FCSTD DOCUMENT  (FreeCAD 2022.709R28846 (Git))
Label: footprint_LED_matrix_8x8
License: Other
objects: Sketcher::SketchObject×5, App::Annotation×2, App::DocumentObjectGroup×1
note: 5 computed .brp shape members not serialized (recipe doc carries the construction recipe); baked Part::Feature solids carry a one-line shape summary decoded from their .brp

FEATURE [Sketcher::SketchObject] Sketch002  label="F_CrtYd_0.05"
  ArcFitTolerance = 0
  FullyConstrained = true
  TreeRank = 2091
  sketch-geometry (4):
    g0: LineSegment StartX=-2.286 StartY=16.764 StartZ=0 EndX=38.862 EndY=16.764 EndZ=0
    g1: LineSegment StartX=38.862 StartY=16.764 StartZ=0 EndX=38.862 EndY=-16.764 EndZ=0
    g2: LineSegment StartX=38.862 StartY=-16.764 StartZ=0 EndX=-2.286 EndY=-16.764 EndZ=0
    g3: LineSegment StartX=-2.286 StartY=-16.764 StartZ=0 EndX=-2.286 EndY=16.764 EndZ=0
  constraints (11):
    c: Coincident(g0,g1)
    c: Coincident(g1,g2)
    c: Coincident(g2,g3)
    c: Coincident(g3,g0)
    c: Horizontal(g0)
    c: Horizontal(g2)
    c: Vertical(g1)
    c: DistanceX(g0,g0) = 41.148
    c: DistanceY(g3,g3) = 33.528
    c: Symmetric(g0,g2,g-1)
    c: Distance(g-1,g3) = 2.286
FEATURE [App::Annotation] Text  label="Ref#_1.0mm"
  LabelText = REF**
  Position = (0,17,0)
  TreeRank = 2095
FEATURE [App::Annotation] Text001  label="Value#_0.8mm"
  LabelText = Value 
  Position = (11,-9,0)
  TreeRank = 2096
FEATURE [Sketcher::SketchObject] Sketch006  label="Pads_NPTH"
  ArcFitTolerance = 0
  FullyConstrained = true
  TreeRank = 2097
  expr: Constraints[9] = 1.6" - 0.16"
  sketch-geometry (4):
    g0: Circle CenterX=0 CenterY=13.97 CenterZ=0 NormalX=0 NormalY=0 NormalZ=1 AngleXU=0 Radius=1
    g1: Circle CenterX=0 CenterY=-13.97 CenterZ=0 NormalX=0 NormalY=0 NormalZ=1 AngleXU=0 Radius=1
    g2: Circle CenterX=36.576 CenterY=13.97 CenterZ=0 NormalX=0 NormalY=0 NormalZ=1 AngleXU=0 Radius=1
    g3: Circle CenterX=36.576 CenterY=-13.97 CenterZ=0 NormalX=0 NormalY=0 NormalZ=1 AngleXU=0 Radius=1
  constraints (11):
    c: Radius(g0) = 1
    c: PointOnObject(g0,g-2)
    c: Equal(g1,g0)
    c: Symmetric(g1,g0,g-1)
    c: Equal(g3,g0)
    c: Equal(g0,g2)
    c: Horizontal(g2,g0)
    c: Horizontal(g1,g3)
    c: Vertical(g2,g3)
    c: DistanceX(g0,g2) = 36.576
    c: DistanceY(g1,g0) = 27.94
FEATURE [Sketcher::SketchObject] Sketch008  label="F_Silks_0.16"
  ArcFitTolerance = 1e-06
  FullyConstrained = false
  TreeRank = 2099
  sketch-geometry (215):
    g0: Circle CenterX=24.2017 CenterY=-2.00747 CenterZ=0 NormalX=0 NormalY=0 NormalZ=-1 AngleXU=5e-16 Radius=1.5
    g1: Circle CenterX=24.2017 CenterY=1.97253 CenterZ=0 NormalX=0 NormalY=0 NormalZ=-1 AngleXU=5e-16 Radius=1.5
    g2: Circle CenterX=20.2217 CenterY=-2.00747 CenterZ=0 NormalX=0 NormalY=0 NormalZ=-1 AngleXU=5e-16 Radius=1.5
    g3: Circle CenterX=20.2217 CenterY=1.97253 CenterZ=0 NormalX=0 NormalY=0 NormalZ=-1 AngleXU=5e-16 Radius=1.5
    g4: Circle CenterX=16.2417 CenterY=-2.00747 CenterZ=0 NormalX=0 NormalY=0 NormalZ=-1 AngleXU=5e-16 Radius=1.5
    g5: Circle CenterX=16.2417 CenterY=1.97253 CenterZ=0 NormalX=0 NormalY=0 NormalZ=-1 AngleXU=5e-16 Radius=1.5
    g6: Circle CenterX=12.2617 CenterY=-2.00747 CenterZ=0 NormalX=0 NormalY=0 NormalZ=-1 AngleXU=5e-16 Radius=1.5
    g7: Circle CenterX=12.2617 CenterY=1.97253 CenterZ=0 NormalX=0 NormalY=0 NormalZ=-1 AngleXU=5e-16 Radius=1.5
    g8: Circle CenterX=8.2817 CenterY=-2.00747 CenterZ=0 NormalX=0 NormalY=0 NormalZ=-1 AngleXU=5e-16 Radius=1.5
    g9: Circle CenterX=8.2817 CenterY=1.97253 CenterZ=0 NormalX=0 NormalY=0 NormalZ=-1 AngleXU=5e-16 Radius=1.5
    g10: Ellipse CenterX=11.8642 CenterY=11.9994 CenterZ=0 NormalX=0 NormalY=0 NormalZ=-1 MajorRadius=0.4 MinorRadius=0.4 AngleXU=2.04918
    g11: Ellipse CenterX=16.9442 CenterY=11.9994 CenterZ=0 NormalX=0 NormalY=0 NormalZ=-1 MajorRadius=0.4 MinorRadius=0.4 AngleXU=2.04918
    g12: Ellipse CenterX=22.0242 CenterY=11.9994 CenterZ=0 NormalX=0 NormalY=0 NormalZ=-1 MajorRadius=0.4 MinorRadius=0.4 AngleXU=2.04918
    g13: Ellipse CenterX=27.1042 CenterY=11.9994 CenterZ=0 NormalX=0 NormalY=0 NormalZ=-1 MajorRadius=0.4 MinorRadius=0.4 AngleXU=2.04918
    g14: Ellipse CenterX=24.5642 CenterY=-12.0006 CenterZ=0 NormalX=0 NormalY=0 NormalZ=-1 MajorRadius=0.4 MinorRadius=0.4 AngleXU=2.04918
    g15: Ellipse CenterX=16.9442 CenterY=-12.0006 CenterZ=0 NormalX=0 NormalY=0 NormalZ=-1 MajorRadius=0.4 MinorRadius=0.4 AngleXU=2.04918
    g16: Ellipse CenterX=11.8642 CenterY=-12.0006 CenterZ=0 NormalX=0 NormalY=0 NormalZ=-1 MajorRadius=0.4 MinorRadius=0.4 AngleXU=2.04918
    g17: Ellipse CenterX=9.3242 CenterY=-12.0006 CenterZ=0 NormalX=0 NormalY=0 NormalZ=-1 MajorRadius=0.4 MinorRadius=0.4 AngleXU=2.04918
    g18: Ellipse CenterX=14.4042 CenterY=-12.0006 CenterZ=0 NormalX=0 NormalY=0 NormalZ=-1 MajorRadius=0.4 MinorRadius=0.4 AngleXU=2.04918
    g19: Ellipse CenterX=19.4842 CenterY=-12.0006 CenterZ=0 NormalX=0 NormalY=0 NormalZ=-1 MajorRadius=0.4 MinorRadius=0.4 AngleXU=2.04918
    g20: Ellipse CenterX=22.0242 CenterY=-12.0006 CenterZ=0 NormalX=0 NormalY=0 NormalZ=-1 MajorRadius=0.4 MinorRadius=0.4 AngleXU=2.04918
    g21: Ellipse CenterX=27.1042 CenterY=-12.0006 CenterZ=0 NormalX=0 NormalY=0 NormalZ=-1 MajorRadius=0.4 MinorRadius=0.4 AngleXU=2.04918
    g22: Ellipse CenterX=24.5642 CenterY=11.9994 CenterZ=0 NormalX=0 NormalY=0 NormalZ=-1 MajorRadius=0.4 MinorRadius=0.4 AngleXU=2.04918
    g23: Ellipse CenterX=19.4842 CenterY=11.9994 CenterZ=0 NormalX=0 NormalY=0 NormalZ=-1 MajorRadius=0.4 MinorRadius=0.4 AngleXU=2.04918
    g24: Ellipse CenterX=14.4042 CenterY=11.9994 CenterZ=0 NormalX=0 NormalY=0 NormalZ=-1 MajorRadius=0.4 MinorRadius=0.4 AngleXU=2.04918
    g25: Ellipse CenterX=9.3242 CenterY=11.9994 CenterZ=0 NormalX=0 NormalY=0 NormalZ=-1 MajorRadius=0.4 MinorRadius=0.4 AngleXU=2.04918
    g26: LineSegment StartX=10.2142 StartY=3.79939 StartZ=0 EndX=10.2142 EndY=4.99939 EndZ=0
    g27: LineSegment StartX=9.7042 StartY=4.99939 StartZ=0 EndX=9.7042 EndY=3.79939 EndZ=0
    g28: LineSegment StartX=10.2142 StartY=4.99939 StartZ=0 EndX=9.7042 EndY=4.99939 EndZ=0
    g29: LineSegment StartX=11.4842 StartY=3.79939 StartZ=0 EndX=11.4842 EndY=4.99939 EndZ=0
    g30: LineSegment StartX=10.9742 StartY=4.99939 StartZ=0 EndX=10.9742 EndY=3.79939 EndZ=0
    g31: LineSegment StartX=11.4842 StartY=4.99939 StartZ=0 EndX=10.9742 EndY=4.99939 EndZ=0
    g32: LineSegment StartX=12.7542 StartY=3.79939 StartZ=0 EndX=12.7542 EndY=4.99939 EndZ=0
    g33: LineSegment StartX=12.2442 StartY=4.99939 StartZ=0 EndX=12.2442 EndY=3.79939 EndZ=0
    g34: LineSegment StartX=12.7542 StartY=4.99939 StartZ=0 EndX=12.2442 EndY=4.99939 EndZ=0
    g35: LineSegment StartX=14.0242 StartY=3.79939 StartZ=0 EndX=14.0242 EndY=4.99939 EndZ=0
    g36: LineSegment StartX=13.5142 StartY=4.99939 StartZ=0 EndX=13.5142 EndY=3.79939 EndZ=0
    g37: LineSegment StartX=14.0242 StartY=4.99939 StartZ=0 EndX=13.5142 EndY=4.99939 EndZ=0
    g38: LineSegment StartX=15.2942 StartY=3.79939 StartZ=0 EndX=15.2942 EndY=4.99939 EndZ=0
    g39: LineSegment StartX=14.7842 StartY=4.99939 StartZ=0 EndX=14.7842 EndY=3.79939 EndZ=0
    g40: LineSegment StartX=15.2942 StartY=4.99939 StartZ=0 EndX=14.7842 EndY=4.99939 EndZ=0
    g41: LineSegment StartX=16.5642 StartY=3.79939 StartZ=0 EndX=16.5642 EndY=4.99939 EndZ=0
    g42: LineSegment StartX=16.0542 StartY=4.99939 StartZ=0 EndX=16.0542 EndY=3.79939 EndZ=0
    g43: LineSegment StartX=16.5642 StartY=4.99939 StartZ=0 EndX=16.0542 EndY=4.99939 EndZ=0
    g44: LineSegment StartX=17.8342 StartY=3.79939 StartZ=0 EndX=17.8342 EndY=4.99939 EndZ=0
    g45: LineSegment StartX=17.3242 StartY=4.99939 StartZ=0 EndX=17.3242 EndY=3.79939 EndZ=0
    g46: LineSegment StartX=17.8342 StartY=4.99939 StartZ=0 EndX=17.3242 EndY=4.99939 EndZ=0
    g47: LineSegment StartX=19.1042 StartY=3.79939 StartZ=0 EndX=19.1042 EndY=4.99939 EndZ=0
    g48: LineSegment StartX=18.5942 StartY=4.99939 StartZ=0 EndX=18.5942 EndY=3.79939 EndZ=0
    g49: LineSegment StartX=19.1042 StartY=4.99939 StartZ=0 EndX=18.5942 EndY=4.99939 EndZ=0
    g50: LineSegment StartX=20.3742 StartY=3.79939 StartZ=0 EndX=20.3742 EndY=4.99939 EndZ=0
    g51: LineSegment StartX=19.8642 StartY=4.99939 StartZ=0 EndX=19.8642 EndY=3.79939 EndZ=0
    g52: LineSegment StartX=20.3742 StartY=4.99939 StartZ=0 EndX=19.8642 EndY=4.99939 EndZ=0
    g53: LineSegment StartX=21.6442 StartY=3.79939 StartZ=0 EndX=21.6442 EndY=4.99939 EndZ=0
    g54: LineSegment StartX=21.1342 StartY=4.99939 StartZ=0 EndX=21.1342 EndY=3.79939 EndZ=0
    g55: LineSegment StartX=21.6442 StartY=4.99939 StartZ=0 EndX=21.1342 EndY=4.99939 EndZ=0
    g56: LineSegment StartX=22.9142 StartY=3.79939 StartZ=0 EndX=22.9142 EndY=4.99939 EndZ=0
    g57: LineSegment StartX=22.4042 StartY=4.99939 StartZ=0 EndX=22.4042 EndY=3.79939 EndZ=0
    g58: LineSegment StartX=22.9142 StartY=4.99939 StartZ=0 EndX=22.4042 EndY=4.99939 EndZ=0
    g59: LineSegment StartX=24.1842 StartY=3.79939 StartZ=0 EndX=24.1842 EndY=4.99939 EndZ=0
    g60: LineSegment StartX=23.6742 StartY=4.99939 StartZ=0 EndX=23.6742 EndY=3.79939 EndZ=0
    g61: LineSegment StartX=24.1842 StartY=4.99939 StartZ=0 EndX=23.6742 EndY=4.99939 EndZ=0
    g62: LineSegment StartX=25.4542 StartY=3.79939 StartZ=0 EndX=25.4542 EndY=4.99939 EndZ=0
    g63: LineSegment StartX=24.9442 StartY=4.99939 StartZ=0 EndX=24.9442 EndY=3.79939 EndZ=0
    g64: LineSegment StartX=25.4542 StartY=4.99939 StartZ=0 EndX=24.9442 EndY=4.99939 EndZ=0
    g65: LineSegment StartX=26.7242 StartY=3.79939 StartZ=0 EndX=26.7242 EndY=4.99939 EndZ=0
    g66: LineSegment StartX=26.2142 StartY=4.99939 StartZ=0 EndX=26.2142 EndY=3.79939 EndZ=0
    g67: LineSegment StartX=26.7242 StartY=4.99939 StartZ=0 EndX=26.2142 EndY=4.99939 EndZ=0
    g68: LineSegment StartX=9.7042 StartY=-3.80061 StartZ=0 EndX=9.7042 EndY=-5.00061 EndZ=0
    g69: LineSegment StartX=10.2142 StartY=-5.00061 StartZ=0 EndX=10.2142 EndY=-3.80061 EndZ=0
    g70: LineSegment StartX=9.7042 StartY=-5.00061 StartZ=0 EndX=10.2142 EndY=-5.00061 EndZ=0
    g71: LineSegment StartX=10.9742 StartY=-3.80061 StartZ=0 EndX=10.9742 EndY=-5.00061 EndZ=0
    g72: LineSegment StartX=11.4842 StartY=-5.00061 StartZ=0 EndX=11.4842 EndY=-3.80061 EndZ=0
    g73: LineSegment StartX=10.9742 StartY=-5.00061 StartZ=0 EndX=11.4842 EndY=-5.00061 EndZ=0
    g74: LineSegment StartX=12.2442 StartY=-3.80061 StartZ=0 EndX=12.2442 EndY=-5.00061 EndZ=0
    g75: LineSegment StartX=12.7542 StartY=-5.00061 StartZ=0 EndX=12.7542 EndY=-3.80061 EndZ=0
    g76: LineSegment StartX=12.2442 StartY=-5.00061 StartZ=0 EndX=12.7542 EndY=-5.00061 EndZ=0
    g77: LineSegment StartX=13.5142 StartY=-3.80061 StartZ=0 EndX=13.5142 EndY=-5.00061 EndZ=0
    g78: LineSegment StartX=14.0242 StartY=-5.00061 StartZ=0 EndX=14.0242 EndY=-3.80061 EndZ=0
    g79: LineSegment StartX=13.5142 StartY=-5.00061 StartZ=0 EndX=14.0242 EndY=-5.00061 EndZ=0
    g80: LineSegment StartX=14.7842 StartY=-3.80061 StartZ=0 EndX=14.7842 EndY=-5.00061 EndZ=0
    g81: LineSegment StartX=15.2942 StartY=-5.00061 StartZ=0 EndX=15.2942 EndY=-3.80061 EndZ=0
    g82: LineSegment StartX=14.7842 StartY=-5.00061 StartZ=0 EndX=15.2942 EndY=-5.00061 EndZ=0
    g83: LineSegment StartX=16.0542 StartY=-3.80061 StartZ=0 EndX=16.0542 EndY=-5.00061 EndZ=0
    g84: LineSegment StartX=16.5642 StartY=-5.00061 StartZ=0 EndX=16.5642 EndY=-3.80061 EndZ=0
    g85: LineSegment StartX=16.0542 StartY=-5.00061 StartZ=0 EndX=16.5642 EndY=-5.00061 EndZ=0
    g86: LineSegment StartX=17.3242 StartY=-3.80061 StartZ=0 EndX=17.3242 EndY=-5.00061 EndZ=0
    g87: LineSegment StartX=17.8342 StartY=-5.00061 StartZ=0 EndX=17.8342 EndY=-3.80061 EndZ=0
    g88: LineSegment StartX=17.3242 StartY=-5.00061 StartZ=0 EndX=17.8342 EndY=-5.00061 EndZ=0
    g89: LineSegment StartX=18.5942 StartY=-3.80061 StartZ=0 EndX=18.5942 EndY=-5.00061 EndZ=0
    g90: LineSegment StartX=19.1042 StartY=-5.00061 StartZ=0 EndX=19.1042 EndY=-3.80061 EndZ=0
    g91: LineSegment StartX=18.5942 StartY=-5.00061 StartZ=0 EndX=19.1042 EndY=-5.00061 EndZ=0
    g92: LineSegment StartX=19.8642 StartY=-3.80061 StartZ=0 EndX=19.8642 EndY=-5.00061 EndZ=0
    g93: LineSegment StartX=20.3742 StartY=-5.00061 StartZ=0 EndX=20.3742 EndY=-3.80061 EndZ=0
    g94: LineSegment StartX=19.8642 StartY=-5.00061 StartZ=0 EndX=20.3742 EndY=-5.00061 EndZ=0
    g95: LineSegment StartX=21.1342 StartY=-3.80061 StartZ=0 EndX=21.1342 EndY=-5.00061 EndZ=0
    g96: LineSegment StartX=21.6442 StartY=-5.00061 StartZ=0 EndX=21.6442 EndY=-3.80061 EndZ=0
    g97: LineSegment StartX=21.1342 StartY=-5.00061 StartZ=0 EndX=21.6442 EndY=-5.00061 EndZ=0
    g98: LineSegment StartX=22.4042 StartY=-3.80061 StartZ=0 EndX=22.4042 EndY=-5.00061 EndZ=0
    g99: LineSegment StartX=22.9142 StartY=-5.00061 StartZ=0 EndX=22.9142 EndY=-3.80061 EndZ=0
    g100: LineSegment StartX=22.4042 StartY=-5.00061 StartZ=0 EndX=22.9142 EndY=-5.00061 EndZ=0
    g101: LineSegment StartX=23.6742 StartY=-3.80061 StartZ=0 EndX=23.6742 EndY=-5.00061 EndZ=0
    g102: LineSegment StartX=24.1842 StartY=-5.00061 StartZ=0 EndX=24.1842 EndY=-3.80061 EndZ=0
    g103: LineSegment StartX=23.6742 StartY=-5.00061 StartZ=0 EndX=24.1842 EndY=-5.00061 EndZ=0
    g104: LineSegment StartX=24.9442 StartY=-3.80061 StartZ=0 EndX=24.9442 EndY=-5.00061 EndZ=0
    g105: LineSegment StartX=25.4542 StartY=-5.00061 StartZ=0 EndX=25.4542 EndY=-3.80061 EndZ=0
    g106: LineSegment StartX=24.9442 StartY=-5.00061 StartZ=0 EndX=25.4542 EndY=-5.00061 EndZ=0
    g107: LineSegment StartX=26.2142 StartY=-3.80061 StartZ=0 EndX=26.2142 EndY=-5.00061 EndZ=0
    g108: LineSegment StartX=26.7242 StartY=-5.00061 StartZ=0 EndX=26.7242 EndY=-3.80061 EndZ=0
    g109: LineSegment StartX=26.2142 StartY=-5.00061 StartZ=0 EndX=26.7242 EndY=-5.00061 EndZ=0
    g110: Ellipse CenterX=9.8942 CenterY=3.11939 CenterZ=0 NormalX=0 NormalY=0 NormalZ=-1 MajorRadius=0.15 MinorRadius=0.15 AngleXU=2.04918
    g111: LineSegment StartX=27.2142 StartY=-3.80061 StartZ=0 EndX=9.2142 EndY=-3.80061 EndZ=0
    g112: LineSegment StartX=27.2142 StartY=3.79939 StartZ=0 EndX=27.2142 EndY=-3.80061 EndZ=0
    g113: LineSegment StartX=9.2142 StartY=-3.80061 StartZ=0 EndX=9.2142 EndY=3.79939 EndZ=0
    g114: LineSegment StartX=9.2142 StartY=3.79939 StartZ=0 EndX=27.2142 EndY=3.79939 EndZ=0
    g115: Circle CenterX=0 CenterY=-1.27 CenterZ=0 NormalX=0 NormalY=0 NormalZ=-1 AngleXU=0 Radius=0.51
    g116: Circle CenterX=0 CenterY=3.81 CenterZ=0 NormalX=0 NormalY=0 NormalZ=-1 AngleXU=0 Radius=0.51
    g117: Circle CenterX=0 CenterY=1.27 CenterZ=0 NormalX=0 NormalY=0 NormalZ=-1 AngleXU=0 Radius=0.51
    g118: Circle CenterX=0 CenterY=-3.81 CenterZ=0 NormalX=0 NormalY=0 NormalZ=-1 AngleXU=0 Radius=0.51
    g119: Circle CenterX=36.576 CenterY=13.97 CenterZ=0 NormalX=0 NormalY=0 NormalZ=1 AngleXU=-3.14159 Radius=1
    g120: Circle CenterX=36.576 CenterY=-13.97 CenterZ=0 NormalX=0 NormalY=0 NormalZ=1 AngleXU=-3.14159 Radius=1
    g121: Circle CenterX=0 CenterY=13.97 CenterZ=0 NormalX=0 NormalY=0 NormalZ=1 AngleXU=-3.14159 Radius=1
    g122: Circle CenterX=0 CenterY=-13.97 CenterZ=0 NormalX=0 NormalY=0 NormalZ=1 AngleXU=-3.14159 Radius=1
    g123: ArcOfCircle CenterX=36.068 CenterY=13.97 CenterZ=0 NormalX=0 NormalY=0 NormalZ=1 AngleXU=1.5708 Radius=2.54 StartAngle=4.71239 EndAngle=6.28319
    g124: LineSegment StartX=0.508 StartY=16.51 StartZ=0 EndX=36.068 EndY=16.51 EndZ=0
    g125: ArcOfCircle CenterX=0.508 CenterY=13.97 CenterZ=0 NormalX=0 NormalY=0 NormalZ=1 AngleXU=3.14155 Radius=2.54 StartAngle=4.71243 EndAngle=6.28323
    g126: LineSegment StartX=-2.032 StartY=-13.97 StartZ=0 EndX=-2.032 EndY=13.97 EndZ=0
    g127: ArcOfCircle CenterX=0.508 CenterY=-13.97 CenterZ=0 NormalX=0 NormalY=0 NormalZ=1 AngleXU=-1.57084 Radius=2.54 StartAngle=4.71243 EndAngle=6.28323
    g128: LineSegment StartX=36.068 StartY=-16.51 StartZ=0 EndX=0.508 EndY=-16.51 EndZ=0
    g129: ArcOfCircle CenterX=36.068 CenterY=-13.97 CenterZ=0 NormalX=0 NormalY=0 NormalZ=1 AngleXU=-4.36332e-05 Radius=2.54 StartAngle=4.71243 EndAngle=6.28323
    g130: LineSegment StartX=38.608 StartY=13.97 StartZ=0 EndX=38.608 EndY=-13.97 EndZ=0
    g131: LineSegment StartX=34.163 StartY=15.875 StartZ=0 EndX=2.413 EndY=15.875 EndZ=0
    g132: LineSegment StartX=2.413 StartY=15.875 StartZ=0 EndX=2.413 EndY=-15.875 EndZ=0
    g133: LineSegment StartX=2.413 StartY=-15.875 StartZ=0 EndX=34.163 EndY=-15.875 EndZ=0
    g134: LineSegment StartX=34.163 StartY=-15.875 StartZ=0 EndX=34.163 EndY=15.875 EndZ=0
    g135: Circle CenterX=32.288 CenterY=14 CenterZ=0 NormalX=0 NormalY=0 NormalZ=-1 AngleXU=5e-16 Radius=1.5
    g136: Circle CenterX=28.288 CenterY=14 CenterZ=0 NormalX=0 NormalY=0 NormalZ=-1 AngleXU=5e-16 Radius=1.5
    g137: Circle CenterX=24.288 CenterY=14 CenterZ=0 NormalX=0 NormalY=0 NormalZ=-1 AngleXU=5e-16 Radius=1.5
    g138: Circle CenterX=20.288 CenterY=14 CenterZ=0 NormalX=0 NormalY=0 NormalZ=-1 AngleXU=5e-16 Radius=1.5
    g139: Circle CenterX=16.288 CenterY=14 CenterZ=0 NormalX=0 NormalY=0 NormalZ=-1 AngleXU=5e-16 Radius=1.5
    g140: Circle CenterX=12.288 CenterY=14 CenterZ=0 NormalX=0 NormalY=0 NormalZ=-1 AngleXU=5e-16 Radius=1.5
    g141: Circle CenterX=8.288 CenterY=14 CenterZ=0 NormalX=0 NormalY=0 NormalZ=-1 AngleXU=5e-16 Radius=1.5
    g142: Circle CenterX=32.288 CenterY=-14 CenterZ=0 NormalX=0 NormalY=0 NormalZ=-1 AngleXU=5e-16 Radius=1.5
    g143: Circle CenterX=32.288 CenterY=-10 CenterZ=0 NormalX=0 NormalY=0 NormalZ=-1 AngleXU=5e-16 Radius=1.5
    g144: Circle CenterX=32.288 CenterY=-6 CenterZ=0 NormalX=0 NormalY=0 NormalZ=-1 AngleXU=5e-16 Radius=1.5
    g145: Circle CenterX=32.288 CenterY=-2 CenterZ=0 NormalX=0 NormalY=0 NormalZ=-1 AngleXU=5e-16 Radius=1.5
    g146: Circle CenterX=32.288 CenterY=2 CenterZ=0 NormalX=0 NormalY=0 NormalZ=-1 AngleXU=5e-16 Radius=1.5
    g147: Circle CenterX=32.288 CenterY=6 CenterZ=0 NormalX=0 NormalY=0 NormalZ=-1 AngleXU=5e-16 Radius=1.5
    g148: Circle CenterX=32.288 CenterY=10 CenterZ=0 NormalX=0 NormalY=0 NormalZ=-1 AngleXU=5e-16 Radius=1.5
    g149: Circle CenterX=28.288 CenterY=-14 CenterZ=0 NormalX=0 NormalY=0 NormalZ=-1 AngleXU=5e-16 Radius=1.5
    g150: Circle CenterX=28.288 CenterY=-10 CenterZ=0 NormalX=0 NormalY=0 NormalZ=-1 AngleXU=5e-16 Radius=1.5
    g151: Circle CenterX=28.288 CenterY=-6 CenterZ=0 NormalX=0 NormalY=0 NormalZ=-1 AngleXU=5e-16 Radius=1.5
    g152: Circle CenterX=28.288 CenterY=-2 CenterZ=0 NormalX=0 NormalY=0 NormalZ=-1 AngleXU=5e-16 Radius=1.5
    g153: Circle CenterX=28.288 CenterY=2 CenterZ=0 NormalX=0 NormalY=0 NormalZ=-1 AngleXU=5e-16 Radius=1.5
    g154: Circle CenterX=28.288 CenterY=6 CenterZ=0 NormalX=0 NormalY=0 NormalZ=-1 AngleXU=5e-16 Radius=1.5
    g155: Circle CenterX=28.288 CenterY=10 CenterZ=0 NormalX=0 NormalY=0 NormalZ=-1 AngleXU=5e-16 Radius=1.5
    g156: Circle CenterX=24.288 CenterY=-14 CenterZ=0 NormalX=0 NormalY=0 NormalZ=-1 AngleXU=5e-16 Radius=1.5
    g157: Circle CenterX=24.288 CenterY=-10 CenterZ=0 NormalX=0 NormalY=0 NormalZ=-1 AngleXU=5e-16 Radius=1.5
    g158: Circle CenterX=24.288 CenterY=-6 CenterZ=0 NormalX=0 NormalY=0 NormalZ=-1 AngleXU=5e-16 Radius=1.5
    g159: Circle CenterX=24.288 CenterY=-2 CenterZ=0 NormalX=0 NormalY=0 NormalZ=-1 AngleXU=5e-16 Radius=1.5
    g160: Circle CenterX=24.288 CenterY=2 CenterZ=0 NormalX=0 NormalY=0 NormalZ=-1 AngleXU=5e-16 Radius=1.5
    g161: Circle CenterX=24.288 CenterY=6 CenterZ=0 NormalX=0 NormalY=0 NormalZ=-1 AngleXU=5e-16 Radius=1.5
    g162: Circle CenterX=24.288 CenterY=10 CenterZ=0 NormalX=0 NormalY=0 NormalZ=-1 AngleXU=5e-16 Radius=1.5
    g163: Circle CenterX=20.288 CenterY=-14 CenterZ=0 NormalX=0 NormalY=0 NormalZ=-1 AngleXU=5e-16 Radius=1.5
    g164: Circle CenterX=20.288 CenterY=-10 CenterZ=0 NormalX=0 NormalY=0 NormalZ=-1 AngleXU=5e-16 Radius=1.5
    g165: Circle CenterX=20.288 CenterY=-6 CenterZ=0 NormalX=0 NormalY=0 NormalZ=-1 AngleXU=5e-16 Radius=1.5
    g166: Circle CenterX=20.288 CenterY=-2 CenterZ=0 NormalX=0 NormalY=0 NormalZ=-1 AngleXU=5e-16 Radius=1.5
    g167: Circle CenterX=20.288 CenterY=2 CenterZ=0 NormalX=0 NormalY=0 NormalZ=-1 AngleXU=5e-16 Radius=1.5
    g168: Circle CenterX=20.288 CenterY=6 CenterZ=0 NormalX=0 NormalY=0 NormalZ=-1 AngleXU=5e-16 Radius=1.5
    g169: Circle CenterX=20.288 CenterY=10 CenterZ=0 NormalX=0 NormalY=0 NormalZ=-1 AngleXU=5e-16 Radius=1.5
    g170: Circle CenterX=16.288 CenterY=-14 CenterZ=0 NormalX=0 NormalY=0 NormalZ=-1 AngleXU=5e-16 Radius=1.5
    g171: Circle CenterX=16.288 CenterY=-10 CenterZ=0 NormalX=0 NormalY=0 NormalZ=-1 AngleXU=5e-16 Radius=1.5
    g172: Circle CenterX=16.288 CenterY=-6 CenterZ=0 NormalX=0 NormalY=0 NormalZ=-1 AngleXU=5e-16 Radius=1.5
    g173: Circle CenterX=16.288 CenterY=-2 CenterZ=0 NormalX=0 NormalY=0 NormalZ=-1 AngleXU=5e-16 Radius=1.5
    g174: Circle CenterX=16.288 CenterY=2 CenterZ=0 NormalX=0 NormalY=0 NormalZ=-1 AngleXU=5e-16 Radius=1.5
    g175: Circle CenterX=16.288 CenterY=6 CenterZ=0 NormalX=0 NormalY=0 NormalZ=-1 AngleXU=5e-16 Radius=1.5
    g176: Circle CenterX=16.288 CenterY=10 CenterZ=0 NormalX=0 NormalY=0 NormalZ=-1 AngleXU=5e-16 Radius=1.5
    g177: Circle CenterX=12.288 CenterY=-14 CenterZ=0 NormalX=0 NormalY=0 NormalZ=-1 AngleXU=5e-16 Radius=1.5
    g178: Circle CenterX=12.288 CenterY=-10 CenterZ=0 NormalX=0 NormalY=0 NormalZ=-1 AngleXU=5e-16 Radius=1.5
    g179: Circle CenterX=12.288 CenterY=-6 CenterZ=0 NormalX=0 NormalY=0 NormalZ=-1 AngleXU=5e-16 Radius=1.5
    g180: Circle CenterX=12.288 CenterY=-2 CenterZ=0 NormalX=0 NormalY=0 NormalZ=-1 AngleXU=5e-16 Radius=1.5
    g181: Circle CenterX=12.288 CenterY=2 CenterZ=0 NormalX=0 NormalY=0 NormalZ=-1 AngleXU=5e-16 Radius=1.5
    g182: Circle CenterX=12.288 CenterY=6 CenterZ=0 NormalX=0 NormalY=0 NormalZ=-1 AngleXU=5e-16 Radius=1.5
    g183: Circle CenterX=12.288 CenterY=10 CenterZ=0 NormalX=0 NormalY=0 NormalZ=-1 AngleXU=5e-16 Radius=1.5
    g184: Circle CenterX=8.288 CenterY=-14 CenterZ=0 NormalX=0 NormalY=0 NormalZ=-1 AngleXU=5e-16 Radius=1.5
    g185: Circle CenterX=8.288 CenterY=-10 CenterZ=0 NormalX=0 NormalY=0 NormalZ=-1 AngleXU=5e-16 Radius=1.5
    g186: Circle CenterX=8.288 CenterY=-6 CenterZ=0 NormalX=0 NormalY=0 NormalZ=-1 AngleXU=5e-16 Radius=1.5
    g187: Circle CenterX=8.288 CenterY=-2 CenterZ=0 NormalX=0 NormalY=0 NormalZ=-1 AngleXU=5e-16 Radius=1.5
    g188: Circle CenterX=8.288 CenterY=2 CenterZ=0 NormalX=0 NormalY=0 NormalZ=-1 AngleXU=5e-16 Radius=1.5
    g189: Circle CenterX=8.288 CenterY=6 CenterZ=0 NormalX=0 NormalY=0 NormalZ=-1 AngleXU=5e-16 Radius=1.5
    g190: Circle CenterX=8.288 CenterY=10 CenterZ=0 NormalX=0 NormalY=0 NormalZ=-1 AngleXU=5e-16 Radius=1.5
    g191: Circle CenterX=4.288 CenterY=-14 CenterZ=0 NormalX=0 NormalY=0 NormalZ=-1 AngleXU=5e-16 Radius=1.5
    g192: Circle CenterX=4.288 CenterY=-10 CenterZ=0 NormalX=0 NormalY=0 NormalZ=-1 AngleXU=5e-16 Radius=1.5
    g193: Circle CenterX=4.288 CenterY=-6 CenterZ=0 NormalX=0 NormalY=0 NormalZ=-1 AngleXU=5e-16 Radius=1.5
    g194: Circle CenterX=4.288 CenterY=-2 CenterZ=0 NormalX=0 NormalY=0 NormalZ=-1 AngleXU=5e-16 Radius=1.5
    g195: Circle CenterX=4.288 CenterY=2 CenterZ=0 NormalX=0 NormalY=0 NormalZ=-1 AngleXU=5e-16 Radius=1.5
    g196: Circle CenterX=4.288 CenterY=6 CenterZ=0 NormalX=0 NormalY=0 NormalZ=-1 AngleXU=5e-16 Radius=1.5
    g197: Circle CenterX=4.288 CenterY=10 CenterZ=0 NormalX=0 NormalY=0 NormalZ=-1 AngleXU=5e-16 Radius=1.5
    g198: Circle CenterX=4.288 CenterY=14 CenterZ=0 NormalX=0 NormalY=0 NormalZ=-1 AngleXU=5e-16 Radius=1.5
    g199: LineSegment [constr] StartX=4.288 StartY=-14 StartZ=0 EndX=4.288 EndY=-10 EndZ=0
    g200: LineSegment [constr] StartX=4.288 StartY=-10 StartZ=0 EndX=4.288 EndY=-6 EndZ=0
    g201: LineSegment [constr] StartX=4.288 StartY=-2 StartZ=0 EndX=4.288 EndY=2 EndZ=0
    g202: LineSegment [constr] StartX=4.288 StartY=2 StartZ=0 EndX=4.288 EndY=6 EndZ=0
    g203: LineSegment [constr] StartX=4.288 StartY=6 StartZ=0 EndX=4.288 EndY=10 EndZ=0
    g204: LineSegment [constr] StartX=4.288 StartY=10 StartZ=0 EndX=4.288 EndY=14 EndZ=0
    g205: LineSegment [constr] StartX=4.288 StartY=14 StartZ=0 EndX=8.288 EndY=14 EndZ=0
    g206: LineSegment [constr] StartX=8.288 StartY=14 StartZ=0 EndX=12.288 EndY=14 EndZ=0
    g207: LineSegment [constr] StartX=12.288 StartY=14 StartZ=0 EndX=16.288 EndY=14 EndZ=0
    g208: LineSegment [constr] StartX=16.288 StartY=14 StartZ=0 EndX=20.288 EndY=14 EndZ=0
    g209: LineSegment [constr] StartX=20.288 StartY=14 StartZ=0 EndX=24.288 EndY=14 EndZ=0
    g210: LineSegment [constr] StartX=24.288 StartY=14 StartZ=0 EndX=28.288 EndY=14 EndZ=0
    g211: LineSegment [constr] StartX=28.288 StartY=14 StartZ=0 EndX=32.288 EndY=14 EndZ=0
    g212: LineSegment [constr] StartX=4.288 StartY=-14 StartZ=0 EndX=2.413 EndY=-14 EndZ=0
    g213: LineSegment [constr] StartX=4.288 StartY=-14 StartZ=0 EndX=4.288 EndY=-15.875 EndZ=0
    g214: LineSegment [constr] StartX=4.288 StartY=-2 StartZ=0 EndX=4.288 EndY=-6 EndZ=0
  constraints (277):
    c: Equal(g127,g129)
    c: Equal(g129,g123)
    c: Equal(g123,g125)
    c: Radius(g125) = 2.54
    c: Vertical(g126)
    c: Vertical(g130)
    c: Horizontal(g124)
    c: Tangent(g127,g128) = 1.5708
    c: Tangent(g126,g127) = 1.5708
    c: Tangent(g128,g129) = 1.5708
    c: Tangent(g129,g130) = 1.5708
    c: Tangent(g123,g130) = 1.5708
    c: Tangent(g123,g124) = 1.5708
    c: Tangent(g124,g125) = 1.5708
    c: Tangent(g125,g126) = 1.5708
    c: DistanceX(g125,g123) = 40.64
    c: DistanceY(g127,g124) = 33.02
    c: Symmetric(g124,g127,g-1)
    c: Distance(g-1,g126) = 2.032
    c: Diameter(g116) = 1.02
    c: Equal(g116,g117)
    c: Equal(g116,g115)
    c: Equal(g116,g118)
    c: Vertical(g116,g117)
    c: Vertical(g115,g118)
    c: DistanceY(g118,g115) = 2.54
    c: DistanceY(g115,g117) = 2.54
    c: DistanceY(g117,g116) = 2.54
    c: Symmetric(g117,g115,g-1)
    c: PointOnObject(g117,g-2)
    c: Diameter(g121) = 2
    c: Equal(g121,g119)
    c: Equal(g121,g120)
    c: Equal(g121,g122)
    c: Horizontal(g122,g120)
    c: Vertical(g120,g119)
    c: Horizontal(g119,g121)
    c: Symmetric(g122,g121,g-1)
    c: PointOnObject(g121,g-2)
    c: DistanceY(g122,g121) = 27.94
    c: Distance(g120,g130) = 2.032
    c: Diameter(g198) = 3
    c: Equal(g198,g141)
    c: Equal(g198,g140)
    c: Equal(g198,g139)
    c: Equal(g198,g138)
    c: Equal(g198,g137)
    c: Equal(g198,g136)
    c: Equal(g198,g135)
    c: Equal(g198,g148)
    c: Equal(g198,g155)
    c: Equal(g198,g162)
    c: Equal(g198,g169)
    c: Equal(g198,g176)
    c: Equal(g198,g183)
    c: Equal(g198,g190)
    c: Equal(g198,g197)
    c: Equal(g198,g196)
    c: Equal(g198,g189)
    c: Equal(g198,g182)
    c: Equal(g198,g175)
    c: Equal(g198,g168)
    c: Equal(g198,g161)
    c: Equal(g198,g154)
    c: Equal(g198,g147)
    c: Equal(g198,g146)
    c: Equal(g198,g153)
    c: Equal(g198,g160)
    c: Equal(g198,g167)
    c: Equal(g198,g174)
    c: Equal(g198,g181)
    c: Equal(g198,g188)
    c: Equal(g198,g195)
    c: Equal(g198,g194)
    c: Equal(g198,g187)
    c: Equal(g198,g180)
    c: Equal(g198,g173)
    c: Equal(g198,g166)
    c: Equal(g198,g159)
    c: Equal(g198,g152)
    c: Equal(g198,g145)
    c: Equal(g198,g144)
    c: Equal(g198,g151)
    c: Equal(g198,g158)
    c: Equal(g198,g165)
    c: Equal(g198,g172)
    c: Equal(g198,g179)
    c: Equal(g198,g186)
    c: Equal(g198,g193)
    c: Equal(g198,g192)
    c: Equal(g198,g185)
    c: Equal(g198,g178)
    c: Equal(g198,g171)
    c: Equal(g198,g164)
    c: Equal(g198,g157)
    c: Equal(g198,g150)
    c: Equal(g198,g143)
    c: Equal(g198,g142)
    c: Equal(g198,g149)
    c: Equal(g198,g156)
    c: Equal(g198,g163)
    c: Equal(g198,g170)
    c: Equal(g198,g177)
    c: Equal(g198,g184)
    c: Equal(g198,g191)
    c: Coincident(g199,g191)
    c: Coincident(g199,g192)
    c: Vertical(g199)
    c: Coincident(g200,g192)
    c: Coincident(g200,g193)
    c: Vertical(g200)
    c: Coincident(g201,g194)
    c: Coincident(g201,g195)
    c: Coincident(g202,g195)
    c: Coincident(g202,g196)
    c: Vertical(g202)
    c: Coincident(g203,g196)
    c: Coincident(g203,g197)
    c: Vertical(g203)
    c: Coincident(g204,g197)
    c: Coincident(g204,g198)
    c: Vertical(g204)
    c: Coincident(g205,g198)
    c: Coincident(g205,g141)
    c: Horizontal(g205)
    c: Coincident(g206,g141)
    c: Coincident(g206,g140)
    c: Horizontal(g206)
    c: Coincident(g207,g140)
    c: Coincident(g207,g139)
    c: Coincident(g208,g139)
    c: Coincident(g208,g138)
    c: Horizontal(g208)
    c: Coincident(g209,g138)
    c: Coincident(g209,g137)
    c: Coincident(g210,g137)
    c: Coincident(g210,g136)
    c: Horizontal(g210)
    c: Coincident(g211,g136)
    c: Coincident(g211,g135)
    c: Horizontal(g211)
    c: Equal(g199,g200)
    c: Equal(g201,g202)
    c: Equal(g202,g203)
    c: Equal(g203,g204)
    c: Equal(g205,g206)
    c: Equal(g206,g207)
    c: Equal(g207,g208)
    c: Equal(g208,g209)
    c: Equal(g209,g210)
    c: Equal(g210,g211)
    c: Symmetric(g194,g195,g-1)
    c: DistanceY(g201,g201) = 4
    c: DistanceX(g205,g205) = 4
    c: Vertical(g184,g185)
    c: Vertical(g185,g186)
    c: Vertical(g186,g187)
    c: Vertical(g187,g188)
    c: Vertical(g188,g189)
    c: Vertical(g189,g190)
    c: Vertical(g190,g141)
    c: Vertical(g140,g183)
    c: Vertical(g183,g182)
    c: Vertical(g182,g181)
    c: Vertical(g181,g180)
    c: Vertical(g180,g179)
    c: Vertical(g179,g178)
    c: Vertical(g178,g177)
    c: Vertical(g139,g176)
    c: Vertical(g176,g175)
    c: Vertical(g175,g174)
    c: Vertical(g174,g173)
    c: Vertical(g173,g172)
    c: Vertical(g172,g171)
    c: Vertical(g171,g170)
    c: Vertical(g138,g169)
    c: Vertical(g169,g168)
    c: Vertical(g168,g167)
    c: Vertical(g167,g166)
    c: Vertical(g166,g165)
    c: Vertical(g165,g164)
    c: Vertical(g164,g163)
    c: Vertical(g137,g162)
    c: Vertical(g162,g161)
    c: Vertical(g161,g160)
    c: Vertical(g160,g159)
    c: Vertical(g159,g158)
    c: Vertical(g158,g157)
    c: Vertical(g157,g156)
    c: Vertical(g136,g155)
    c: Vertical(g155,g154)
    c: Vertical(g154,g153)
    c: Vertical(g153,g152)
    c: Vertical(g152,g151)
    c: Vertical(g151,g150)
    c: Vertical(g150,g149)
    c: Vertical(g135,g148)
    c: Vertical(g148,g147)
    c: Vertical(g147,g146)
    c: Vertical(g146,g145)
    c: Vertical(g145,g144)
    c: Vertical(g144,g143)
    c: Vertical(g143,g142)
    c: Horizontal(g197,g190)
    c: Horizontal(g190,g183)
    c: Horizontal(g183,g176)
    c: Horizontal(g176,g169)
    c: Horizontal(g169,g162)
    c: Horizontal(g162,g155)
    c: Horizontal(g155,g148)
    c: Horizontal(g196,g189)
    c: Horizontal(g189,g182)
    c: Horizontal(g182,g175)
    c: Horizontal(g175,g168)
    c: Horizontal(g168,g161)
    c: Horizontal(g161,g154)
    c: Horizontal(g154,g147)
    c: Horizontal(g195,g188)
    c: Horizontal(g188,g181)
    c: Horizontal(g181,g174)
    c: Horizontal(g174,g167)
    c: Horizontal(g167,g160)
    c: Horizontal(g160,g153)
    c: Horizontal(g153,g146)
    c: Horizontal(g194,g187)
    c: Horizontal(g187,g180)
    c: Horizontal(g180,g173)
    c: Horizontal(g173,g166)
    c: Horizontal(g166,g159)
    c: Horizontal(g159,g152)
    c: Horizontal(g152,g145)
    c: Horizontal(g193,g186)
    c: Horizontal(g186,g179)
    c: Horizontal(g179,g172)
    c: Horizontal(g172,g165)
    c: Horizontal(g165,g158)
    c: Horizontal(g158,g151)
    c: Horizontal(g151,g144)
    c: Horizontal(g192,g185)
    c: Horizontal(g185,g178)
    c: Horizontal(g178,g171)
    c: Horizontal(g171,g164)
    c: Horizontal(g164,g157)
    c: Horizontal(g157,g150)
    c: Horizontal(g150,g143)
    c: Horizontal(g191,g184)
    c: Horizontal(g184,g177)
    c: Horizontal(g177,g170)
    c: Horizontal(g170,g163)
    c: Horizontal(g163,g156)
    c: Horizontal(g156,g149)
    c: Horizontal(g149,g142)
    c: Coincident(g131,g132)
    c: Horizontal(g131)
    c: Coincident(g132,g133)
    c: Horizontal(g133)
    c: Coincident(g133,g134)
    c: Vertical(g134)
    c: Coincident(g131,g134)
    c: Equal(g132,g131)
    c: DistanceY(g132,g132) = 31.75
    c: Symmetric(g131,g132,g-1)
    c: Coincident(g212,g191)
    c: PointOnObject(g212,g132)
    c: Coincident(g213,g191)
    c: PointOnObject(g213,g133)
    c: Vertical(g213)
    c: Horizontal(g212)
    c: Equal(g212,g213)
    c: DistanceX(g212,g212) = 1.875
    c: Coincident(g214,g194)
    c: Coincident(g214,g193)
    c: Vertical(g214)
    c: Horizontal(g207)
    c: Horizontal(g209)
    c: DistanceX(g125,g131) = 4.445
    c: Equal(g201,g214)
FEATURE [Sketcher::SketchObject] Sketch009  label="Pads_TH_SMD"
  ArcFitTolerance = 0
  FullyConstrained = true
  TreeRank = 2144
  sketch-geometry (8):
    g0: Circle CenterX=0 CenterY=1.27 CenterZ=0 NormalX=0 NormalY=0 NormalZ=1 AngleXU=0 Radius=0.5
    g1: Circle CenterX=0 CenterY=1.27 CenterZ=0 NormalX=0 NormalY=0 NormalZ=1 AngleXU=0 Radius=0.9
    g2: Circle CenterX=0 CenterY=-1.27 CenterZ=0 NormalX=0 NormalY=0 NormalZ=1 AngleXU=0 Radius=0.5
    g3: Circle CenterX=0 CenterY=-1.27 CenterZ=0 NormalX=0 NormalY=0 NormalZ=1 AngleXU=0 Radius=0.9
    g4: Circle CenterX=0 CenterY=-3.81 CenterZ=0 NormalX=0 NormalY=0 NormalZ=1 AngleXU=0 Radius=0.5
    g5: Circle CenterX=0 CenterY=-3.81 CenterZ=0 NormalX=0 NormalY=0 NormalZ=1 AngleXU=0 Radius=0.9
    g6: Circle CenterX=0 CenterY=3.81 CenterZ=0 NormalX=0 NormalY=0 NormalZ=1 AngleXU=0 Radius=0.5
    g7: Circle CenterX=0 CenterY=3.81 CenterZ=0 NormalX=0 NormalY=0 NormalZ=1 AngleXU=0 Radius=0.9
  constraints (18):
    c: Diameter(g0) = 1
    c: Diameter(g1) = 1.8
    c: DistanceX(g0,g-1) = 0
    c: Coincident(g0,g1)
    c: DistanceY(g-1,g0) = 1.27
    c: Equal(g3,g1)
    c: Equal(g2,g0)
    c: Coincident(g2,g3)
    c: Symmetric(g2,g0,g-1)
    c: Equal(g4,g0)
    c: Equal(g5,g1)
    c: Coincident(g4,g5)
    c: PointOnObject(g4,g-2)
    c: DistanceY(g4,g2) = 2.54
    c: Coincident(g6,g7)
    c: Equal(g6,g0)
    c: Equal(g7,g1)
    c: Symmetric(g6,g4,g-1)
FEATURE [Sketcher::SketchObject] Sketch010  label="F_Fab_0.1"
  ArcFitTolerance = 1e-06
  FullyConstrained = false
  TreeRank = 2146
  sketch-geometry (215):
    g0: Circle CenterX=24.2017 CenterY=-2.00747 CenterZ=0 NormalX=0 NormalY=0 NormalZ=-1 AngleXU=5e-16 Radius=1.5
    g1: Circle CenterX=24.2017 CenterY=1.97253 CenterZ=0 NormalX=0 NormalY=0 NormalZ=-1 AngleXU=5e-16 Radius=1.5
    g2: Circle CenterX=20.2217 CenterY=-2.00747 CenterZ=0 NormalX=0 NormalY=0 NormalZ=-1 AngleXU=5e-16 Radius=1.5
    g3: Circle CenterX=20.2217 CenterY=1.97253 CenterZ=0 NormalX=0 NormalY=0 NormalZ=-1 AngleXU=5e-16 Radius=1.5
    g4: Circle CenterX=16.2417 CenterY=-2.00747 CenterZ=0 NormalX=0 NormalY=0 NormalZ=-1 AngleXU=5e-16 Radius=1.5
    g5: Circle CenterX=16.2417 CenterY=1.97253 CenterZ=0 NormalX=0 NormalY=0 NormalZ=-1 AngleXU=5e-16 Radius=1.5
    g6: Circle CenterX=12.2617 CenterY=-2.00747 CenterZ=0 NormalX=0 NormalY=0 NormalZ=-1 AngleXU=5e-16 Radius=1.5
    g7: Circle CenterX=12.2617 CenterY=1.97253 CenterZ=0 NormalX=0 NormalY=0 NormalZ=-1 AngleXU=5e-16 Radius=1.5
    g8: Circle CenterX=8.2817 CenterY=-2.00747 CenterZ=0 NormalX=0 NormalY=0 NormalZ=-1 AngleXU=5e-16 Radius=1.5
    g9: Circle CenterX=8.2817 CenterY=1.97253 CenterZ=0 NormalX=0 NormalY=0 NormalZ=-1 AngleXU=5e-16 Radius=1.5
    g10: Ellipse CenterX=11.8642 CenterY=11.9994 CenterZ=0 NormalX=0 NormalY=0 NormalZ=-1 MajorRadius=0.4 MinorRadius=0.4 AngleXU=2.04918
    g11: Ellipse CenterX=16.9442 CenterY=11.9994 CenterZ=0 NormalX=0 NormalY=0 NormalZ=-1 MajorRadius=0.4 MinorRadius=0.4 AngleXU=2.04918
    g12: Ellipse CenterX=22.0242 CenterY=11.9994 CenterZ=0 NormalX=0 NormalY=0 NormalZ=-1 MajorRadius=0.4 MinorRadius=0.4 AngleXU=2.04918
    g13: Ellipse CenterX=27.1042 CenterY=11.9994 CenterZ=0 NormalX=0 NormalY=0 NormalZ=-1 MajorRadius=0.4 MinorRadius=0.4 AngleXU=2.04918
    g14: Ellipse CenterX=24.5642 CenterY=-12.0006 CenterZ=0 NormalX=0 NormalY=0 NormalZ=-1 MajorRadius=0.4 MinorRadius=0.4 AngleXU=2.04918
    g15: Ellipse CenterX=16.9442 CenterY=-12.0006 CenterZ=0 NormalX=0 NormalY=0 NormalZ=-1 MajorRadius=0.4 MinorRadius=0.4 AngleXU=2.04918
    g16: Ellipse CenterX=11.8642 CenterY=-12.0006 CenterZ=0 NormalX=0 NormalY=0 NormalZ=-1 MajorRadius=0.4 MinorRadius=0.4 AngleXU=2.04918
    g17: Ellipse CenterX=9.3242 CenterY=-12.0006 CenterZ=0 NormalX=0 NormalY=0 NormalZ=-1 MajorRadius=0.4 MinorRadius=0.4 AngleXU=2.04918
    g18: Ellipse CenterX=14.4042 CenterY=-12.0006 CenterZ=0 NormalX=0 NormalY=0 NormalZ=-1 MajorRadius=0.4 MinorRadius=0.4 AngleXU=2.04918
    g19: Ellipse CenterX=19.4842 CenterY=-12.0006 CenterZ=0 NormalX=0 NormalY=0 NormalZ=-1 MajorRadius=0.4 MinorRadius=0.4 AngleXU=2.04918
    g20: Ellipse CenterX=22.0242 CenterY=-12.0006 CenterZ=0 NormalX=0 NormalY=0 NormalZ=-1 MajorRadius=0.4 MinorRadius=0.4 AngleXU=2.04918
    g21: Ellipse CenterX=27.1042 CenterY=-12.0006 CenterZ=0 NormalX=0 NormalY=0 NormalZ=-1 MajorRadius=0.4 MinorRadius=0.4 AngleXU=2.04918
    g22: Ellipse CenterX=24.5642 CenterY=11.9994 CenterZ=0 NormalX=0 NormalY=0 NormalZ=-1 MajorRadius=0.4 MinorRadius=0.4 AngleXU=2.04918
    g23: Ellipse CenterX=19.4842 CenterY=11.9994 CenterZ=0 NormalX=0 NormalY=0 NormalZ=-1 MajorRadius=0.4 MinorRadius=0.4 AngleXU=2.04918
    g24: Ellipse CenterX=14.4042 CenterY=11.9994 CenterZ=0 NormalX=0 NormalY=0 NormalZ=-1 MajorRadius=0.4 MinorRadius=0.4 AngleXU=2.04918
    g25: Ellipse CenterX=9.3242 CenterY=11.9994 CenterZ=0 NormalX=0 NormalY=0 NormalZ=-1 MajorRadius=0.4 MinorRadius=0.4 AngleXU=2.04918
    g26: LineSegment StartX=10.2142 StartY=3.79939 StartZ=0 EndX=10.2142 EndY=4.99939 EndZ=0
    g27: LineSegment StartX=9.7042 StartY=4.99939 StartZ=0 EndX=9.7042 EndY=3.79939 EndZ=0
    g28: LineSegment StartX=10.2142 StartY=4.99939 StartZ=0 EndX=9.7042 EndY=4.99939 EndZ=0
    g29: LineSegment StartX=11.4842 StartY=3.79939 StartZ=0 EndX=11.4842 EndY=4.99939 EndZ=0
    g30: LineSegment StartX=10.9742 StartY=4.99939 StartZ=0 EndX=10.9742 EndY=3.79939 EndZ=0
    g31: LineSegment StartX=11.4842 StartY=4.99939 StartZ=0 EndX=10.9742 EndY=4.99939 EndZ=0
    g32: LineSegment StartX=12.7542 StartY=3.79939 StartZ=0 EndX=12.7542 EndY=4.99939 EndZ=0
    g33: LineSegment StartX=12.2442 StartY=4.99939 StartZ=0 EndX=12.2442 EndY=3.79939 EndZ=0
    g34: LineSegment StartX=12.7542 StartY=4.99939 StartZ=0 EndX=12.2442 EndY=4.99939 EndZ=0
    g35: LineSegment StartX=14.0242 StartY=3.79939 StartZ=0 EndX=14.0242 EndY=4.99939 EndZ=0
    g36: LineSegment StartX=13.5142 StartY=4.99939 StartZ=0 EndX=13.5142 EndY=3.79939 EndZ=0
    g37: LineSegment StartX=14.0242 StartY=4.99939 StartZ=0 EndX=13.5142 EndY=4.99939 EndZ=0
    g38: LineSegment StartX=15.2942 StartY=3.79939 StartZ=0 EndX=15.2942 EndY=4.99939 EndZ=0
    g39: LineSegment StartX=14.7842 StartY=4.99939 StartZ=0 EndX=14.7842 EndY=3.79939 EndZ=0
    g40: LineSegment StartX=15.2942 StartY=4.99939 StartZ=0 EndX=14.7842 EndY=4.99939 EndZ=0
    g41: LineSegment StartX=16.5642 StartY=3.79939 StartZ=0 EndX=16.5642 EndY=4.99939 EndZ=0
    g42: LineSegment StartX=16.0542 StartY=4.99939 StartZ=0 EndX=16.0542 EndY=3.79939 EndZ=0
    g43: LineSegment StartX=16.5642 StartY=4.99939 StartZ=0 EndX=16.0542 EndY=4.99939 EndZ=0
    g44: LineSegment StartX=17.8342 StartY=3.79939 StartZ=0 EndX=17.8342 EndY=4.99939 EndZ=0
    g45: LineSegment StartX=17.3242 StartY=4.99939 StartZ=0 EndX=17.3242 EndY=3.79939 EndZ=0
    g46: LineSegment StartX=17.8342 StartY=4.99939 StartZ=0 EndX=17.3242 EndY=4.99939 EndZ=0
    g47: LineSegment StartX=19.1042 StartY=3.79939 StartZ=0 EndX=19.1042 EndY=4.99939 EndZ=0
    g48: LineSegment StartX=18.5942 StartY=4.99939 StartZ=0 EndX=18.5942 EndY=3.79939 EndZ=0
    g49: LineSegment StartX=19.1042 StartY=4.99939 StartZ=0 EndX=18.5942 EndY=4.99939 EndZ=0
    g50: LineSegment StartX=20.3742 StartY=3.79939 StartZ=0 EndX=20.3742 EndY=4.99939 EndZ=0
    g51: LineSegment StartX=19.8642 StartY=4.99939 StartZ=0 EndX=19.8642 EndY=3.79939 EndZ=0
    g52: LineSegment StartX=20.3742 StartY=4.99939 StartZ=0 EndX=19.8642 EndY=4.99939 EndZ=0
    g53: LineSegment StartX=21.6442 StartY=3.79939 StartZ=0 EndX=21.6442 EndY=4.99939 EndZ=0
    g54: LineSegment StartX=21.1342 StartY=4.99939 StartZ=0 EndX=21.1342 EndY=3.79939 EndZ=0
    g55: LineSegment StartX=21.6442 StartY=4.99939 StartZ=0 EndX=21.1342 EndY=4.99939 EndZ=0
    g56: LineSegment StartX=22.9142 StartY=3.79939 StartZ=0 EndX=22.9142 EndY=4.99939 EndZ=0
    g57: LineSegment StartX=22.4042 StartY=4.99939 StartZ=0 EndX=22.4042 EndY=3.79939 EndZ=0
    g58: LineSegment StartX=22.9142 StartY=4.99939 StartZ=0 EndX=22.4042 EndY=4.99939 EndZ=0
    g59: LineSegment StartX=24.1842 StartY=3.79939 StartZ=0 EndX=24.1842 EndY=4.99939 EndZ=0
    g60: LineSegment StartX=23.6742 StartY=4.99939 StartZ=0 EndX=23.6742 EndY=3.79939 EndZ=0
    g61: LineSegment StartX=24.1842 StartY=4.99939 StartZ=0 EndX=23.6742 EndY=4.99939 EndZ=0
    g62: LineSegment StartX=25.4542 StartY=3.79939 StartZ=0 EndX=25.4542 EndY=4.99939 EndZ=0
    g63: LineSegment StartX=24.9442 StartY=4.99939 StartZ=0 EndX=24.9442 EndY=3.79939 EndZ=0
    g64: LineSegment StartX=25.4542 StartY=4.99939 StartZ=0 EndX=24.9442 EndY=4.99939 EndZ=0
    g65: LineSegment StartX=26.7242 StartY=3.79939 StartZ=0 EndX=26.7242 EndY=4.99939 EndZ=0
    g66: LineSegment StartX=26.2142 StartY=4.99939 StartZ=0 EndX=26.2142 EndY=3.79939 EndZ=0
    g67: LineSegment StartX=26.7242 StartY=4.99939 StartZ=0 EndX=26.2142 EndY=4.99939 EndZ=0
    g68: LineSegment StartX=9.7042 StartY=-3.80061 StartZ=0 EndX=9.7042 EndY=-5.00061 EndZ=0
    g69: LineSegment StartX=10.2142 StartY=-5.00061 StartZ=0 EndX=10.2142 EndY=-3.80061 EndZ=0
    g70: LineSegment StartX=9.7042 StartY=-5.00061 StartZ=0 EndX=10.2142 EndY=-5.00061 EndZ=0
    g71: LineSegment StartX=10.9742 StartY=-3.80061 StartZ=0 EndX=10.9742 EndY=-5.00061 EndZ=0
    g72: LineSegment StartX=11.4842 StartY=-5.00061 StartZ=0 EndX=11.4842 EndY=-3.80061 EndZ=0
    g73: LineSegment StartX=10.9742 StartY=-5.00061 StartZ=0 EndX=11.4842 EndY=-5.00061 EndZ=0
    g74: LineSegment StartX=12.2442 StartY=-3.80061 StartZ=0 EndX=12.2442 EndY=-5.00061 EndZ=0
    g75: LineSegment StartX=12.7542 StartY=-5.00061 StartZ=0 EndX=12.7542 EndY=-3.80061 EndZ=0
    g76: LineSegment StartX=12.2442 StartY=-5.00061 StartZ=0 EndX=12.7542 EndY=-5.00061 EndZ=0
    g77: LineSegment StartX=13.5142 StartY=-3.80061 StartZ=0 EndX=13.5142 EndY=-5.00061 EndZ=0
    g78: LineSegment StartX=14.0242 StartY=-5.00061 StartZ=0 EndX=14.0242 EndY=-3.80061 EndZ=0
    g79: LineSegment StartX=13.5142 StartY=-5.00061 StartZ=0 EndX=14.0242 EndY=-5.00061 EndZ=0
    g80: LineSegment StartX=14.7842 StartY=-3.80061 StartZ=0 EndX=14.7842 EndY=-5.00061 EndZ=0
    g81: LineSegment StartX=15.2942 StartY=-5.00061 StartZ=0 EndX=15.2942 EndY=-3.80061 EndZ=0
    g82: LineSegment StartX=14.7842 StartY=-5.00061 StartZ=0 EndX=15.2942 EndY=-5.00061 EndZ=0
    g83: LineSegment StartX=16.0542 StartY=-3.80061 StartZ=0 EndX=16.0542 EndY=-5.00061 EndZ=0
    g84: LineSegment StartX=16.5642 StartY=-5.00061 StartZ=0 EndX=16.5642 EndY=-3.80061 EndZ=0
    g85: LineSegment StartX=16.0542 StartY=-5.00061 StartZ=0 EndX=16.5642 EndY=-5.00061 EndZ=0
    g86: LineSegment StartX=17.3242 StartY=-3.80061 StartZ=0 EndX=17.3242 EndY=-5.00061 EndZ=0
    g87: LineSegment StartX=17.8342 StartY=-5.00061 StartZ=0 EndX=17.8342 EndY=-3.80061 EndZ=0
    g88: LineSegment StartX=17.3242 StartY=-5.00061 StartZ=0 EndX=17.8342 EndY=-5.00061 EndZ=0
    g89: LineSegment StartX=18.5942 StartY=-3.80061 StartZ=0 EndX=18.5942 EndY=-5.00061 EndZ=0
    g90: LineSegment StartX=19.1042 StartY=-5.00061 StartZ=0 EndX=19.1042 EndY=-3.80061 EndZ=0
    g91: LineSegment StartX=18.5942 StartY=-5.00061 StartZ=0 EndX=19.1042 EndY=-5.00061 EndZ=0
    g92: LineSegment StartX=19.8642 StartY=-3.80061 StartZ=0 EndX=19.8642 EndY=-5.00061 EndZ=0
    g93: LineSegment StartX=20.3742 StartY=-5.00061 StartZ=0 EndX=20.3742 EndY=-3.80061 EndZ=0
    g94: LineSegment StartX=19.8642 StartY=-5.00061 StartZ=0 EndX=20.3742 EndY=-5.00061 EndZ=0
    g95: LineSegment StartX=21.1342 StartY=-3.80061 StartZ=0 EndX=21.1342 EndY=-5.00061 EndZ=0
    g96: LineSegment StartX=21.6442 StartY=-5.00061 StartZ=0 EndX=21.6442 EndY=-3.80061 EndZ=0
    g97: LineSegment StartX=21.1342 StartY=-5.00061 StartZ=0 EndX=21.6442 EndY=-5.00061 EndZ=0
    g98: LineSegment StartX=22.4042 StartY=-3.80061 StartZ=0 EndX=22.4042 EndY=-5.00061 EndZ=0
    g99: LineSegment StartX=22.9142 StartY=-5.00061 StartZ=0 EndX=22.9142 EndY=-3.80061 EndZ=0
    g100: LineSegment StartX=22.4042 StartY=-5.00061 StartZ=0 EndX=22.9142 EndY=-5.00061 EndZ=0
    g101: LineSegment StartX=23.6742 StartY=-3.80061 StartZ=0 EndX=23.6742 EndY=-5.00061 EndZ=0
    g102: LineSegment StartX=24.1842 StartY=-5.00061 StartZ=0 EndX=24.1842 EndY=-3.80061 EndZ=0
    g103: LineSegment StartX=23.6742 StartY=-5.00061 StartZ=0 EndX=24.1842 EndY=-5.00061 EndZ=0
    g104: LineSegment StartX=24.9442 StartY=-3.80061 StartZ=0 EndX=24.9442 EndY=-5.00061 EndZ=0
    g105: LineSegment StartX=25.4542 StartY=-5.00061 StartZ=0 EndX=25.4542 EndY=-3.80061 EndZ=0
    g106: LineSegment StartX=24.9442 StartY=-5.00061 StartZ=0 EndX=25.4542 EndY=-5.00061 EndZ=0
    g107: LineSegment StartX=26.2142 StartY=-3.80061 StartZ=0 EndX=26.2142 EndY=-5.00061 EndZ=0
    g108: LineSegment StartX=26.7242 StartY=-5.00061 StartZ=0 EndX=26.7242 EndY=-3.80061 EndZ=0
    g109: LineSegment StartX=26.2142 StartY=-5.00061 StartZ=0 EndX=26.7242 EndY=-5.00061 EndZ=0
    g110: Ellipse CenterX=9.8942 CenterY=3.11939 CenterZ=0 NormalX=0 NormalY=0 NormalZ=-1 MajorRadius=0.15 MinorRadius=0.15 AngleXU=2.04918
    g111: LineSegment StartX=27.2142 StartY=-3.80061 StartZ=0 EndX=9.2142 EndY=-3.80061 EndZ=0
    g112: LineSegment StartX=27.2142 StartY=3.79939 StartZ=0 EndX=27.2142 EndY=-3.80061 EndZ=0
    g113: LineSegment StartX=9.2142 StartY=-3.80061 StartZ=0 EndX=9.2142 EndY=3.79939 EndZ=0
    g114: LineSegment StartX=9.2142 StartY=3.79939 StartZ=0 EndX=27.2142 EndY=3.79939 EndZ=0
    g115: Circle CenterX=0 CenterY=-1.27 CenterZ=0 NormalX=0 NormalY=0 NormalZ=-1 AngleXU=0 Radius=0.51
    g116: Circle CenterX=0 CenterY=3.81 CenterZ=0 NormalX=0 NormalY=0 NormalZ=-1 AngleXU=0 Radius=0.51
    g117: Circle CenterX=0 CenterY=1.27 CenterZ=0 NormalX=0 NormalY=0 NormalZ=-1 AngleXU=0 Radius=0.51
    g118: Circle CenterX=0 CenterY=-3.81 CenterZ=0 NormalX=0 NormalY=0 NormalZ=-1 AngleXU=0 Radius=0.51
    g119: Circle CenterX=36.576 CenterY=13.97 CenterZ=0 NormalX=0 NormalY=0 NormalZ=1 AngleXU=-3.14159 Radius=1
    g120: Circle CenterX=36.576 CenterY=-13.97 CenterZ=0 NormalX=0 NormalY=0 NormalZ=1 AngleXU=-3.14159 Radius=1
    g121: Circle CenterX=0 CenterY=13.97 CenterZ=0 NormalX=0 NormalY=0 NormalZ=1 AngleXU=-3.14159 Radius=1
    g122: Circle CenterX=0 CenterY=-13.97 CenterZ=0 NormalX=0 NormalY=0 NormalZ=1 AngleXU=-3.14159 Radius=1
    g123: ArcOfCircle CenterX=36.068 CenterY=13.97 CenterZ=0 NormalX=0 NormalY=0 NormalZ=1 AngleXU=1.5708 Radius=2.54 StartAngle=4.71239 EndAngle=6.28319
    g124: LineSegment StartX=0.508 StartY=16.51 StartZ=0 EndX=36.068 EndY=16.51 EndZ=0
    g125: ArcOfCircle CenterX=0.508 CenterY=13.97 CenterZ=0 NormalX=0 NormalY=0 NormalZ=1 AngleXU=3.14155 Radius=2.54 StartAngle=4.71243 EndAngle=6.28323
    g126: LineSegment StartX=-2.032 StartY=-13.97 StartZ=0 EndX=-2.032 EndY=13.97 EndZ=0
    g127: ArcOfCircle CenterX=0.508 CenterY=-13.97 CenterZ=0 NormalX=0 NormalY=0 NormalZ=1 AngleXU=-1.57084 Radius=2.54 StartAngle=4.71243 EndAngle=6.28323
    g128: LineSegment StartX=36.068 StartY=-16.51 StartZ=0 EndX=0.508 EndY=-16.51 EndZ=0
    g129: ArcOfCircle CenterX=36.068 CenterY=-13.97 CenterZ=0 NormalX=0 NormalY=0 NormalZ=1 AngleXU=-4.36332e-05 Radius=2.54 StartAngle=4.71243 EndAngle=6.28323
    g130: LineSegment StartX=38.608 StartY=13.97 StartZ=0 EndX=38.608 EndY=-13.97 EndZ=0
    g131: LineSegment StartX=34.163 StartY=15.875 StartZ=0 EndX=2.413 EndY=15.875 EndZ=0
    g132: LineSegment StartX=2.413 StartY=15.875 StartZ=0 EndX=2.413 EndY=-15.875 EndZ=0
    g133: LineSegment StartX=2.413 StartY=-15.875 StartZ=0 EndX=34.163 EndY=-15.875 EndZ=0
    g134: LineSegment StartX=34.163 StartY=-15.875 StartZ=0 EndX=34.163 EndY=15.875 EndZ=0
    g135: Circle CenterX=32.288 CenterY=14 CenterZ=0 NormalX=0 NormalY=0 NormalZ=-1 AngleXU=5e-16 Radius=1.5
    g136: Circle CenterX=28.288 CenterY=14 CenterZ=0 NormalX=0 NormalY=0 NormalZ=-1 AngleXU=5e-16 Radius=1.5
    g137: Circle CenterX=24.288 CenterY=14 CenterZ=0 NormalX=0 NormalY=0 NormalZ=-1 AngleXU=5e-16 Radius=1.5
    g138: Circle CenterX=20.288 CenterY=14 CenterZ=0 NormalX=0 NormalY=0 NormalZ=-1 AngleXU=5e-16 Radius=1.5
    g139: Circle CenterX=16.288 CenterY=14 CenterZ=0 NormalX=0 NormalY=0 NormalZ=-1 AngleXU=5e-16 Radius=1.5
    g140: Circle CenterX=12.288 CenterY=14 CenterZ=0 NormalX=0 NormalY=0 NormalZ=-1 AngleXU=5e-16 Radius=1.5
    g141: Circle CenterX=8.288 CenterY=14 CenterZ=0 NormalX=0 NormalY=0 NormalZ=-1 AngleXU=5e-16 Radius=1.5
    g142: Circle CenterX=32.288 CenterY=-14 CenterZ=0 NormalX=0 NormalY=0 NormalZ=-1 AngleXU=5e-16 Radius=1.5
    g143: Circle CenterX=32.288 CenterY=-10 CenterZ=0 NormalX=0 NormalY=0 NormalZ=-1 AngleXU=5e-16 Radius=1.5
    g144: Circle CenterX=32.288 CenterY=-6 CenterZ=0 NormalX=0 NormalY=0 NormalZ=-1 AngleXU=5e-16 Radius=1.5
    g145: Circle CenterX=32.288 CenterY=-2 CenterZ=0 NormalX=0 NormalY=0 NormalZ=-1 AngleXU=5e-16 Radius=1.5
    g146: Circle CenterX=32.288 CenterY=2 CenterZ=0 NormalX=0 NormalY=0 NormalZ=-1 AngleXU=5e-16 Radius=1.5
    g147: Circle CenterX=32.288 CenterY=6 CenterZ=0 NormalX=0 NormalY=0 NormalZ=-1 AngleXU=5e-16 Radius=1.5
    g148: Circle CenterX=32.288 CenterY=10 CenterZ=0 NormalX=0 NormalY=0 NormalZ=-1 AngleXU=5e-16 Radius=1.5
    g149: Circle CenterX=28.288 CenterY=-14 CenterZ=0 NormalX=0 NormalY=0 NormalZ=-1 AngleXU=5e-16 Radius=1.5
    g150: Circle CenterX=28.288 CenterY=-10 CenterZ=0 NormalX=0 NormalY=0 NormalZ=-1 AngleXU=5e-16 Radius=1.5
    g151: Circle CenterX=28.288 CenterY=-6 CenterZ=0 NormalX=0 NormalY=0 NormalZ=-1 AngleXU=5e-16 Radius=1.5
    g152: Circle CenterX=28.288 CenterY=-2 CenterZ=0 NormalX=0 NormalY=0 NormalZ=-1 AngleXU=5e-16 Radius=1.5
    g153: Circle CenterX=28.288 CenterY=2 CenterZ=0 NormalX=0 NormalY=0 NormalZ=-1 AngleXU=5e-16 Radius=1.5
    g154: Circle CenterX=28.288 CenterY=6 CenterZ=0 NormalX=0 NormalY=0 NormalZ=-1 AngleXU=5e-16 Radius=1.5
    g155: Circle CenterX=28.288 CenterY=10 CenterZ=0 NormalX=0 NormalY=0 NormalZ=-1 AngleXU=5e-16 Radius=1.5
    g156: Circle CenterX=24.288 CenterY=-14 CenterZ=0 NormalX=0 NormalY=0 NormalZ=-1 AngleXU=5e-16 Radius=1.5
    g157: Circle CenterX=24.288 CenterY=-10 CenterZ=0 NormalX=0 NormalY=0 NormalZ=-1 AngleXU=5e-16 Radius=1.5
    g158: Circle CenterX=24.288 CenterY=-6 CenterZ=0 NormalX=0 NormalY=0 NormalZ=-1 AngleXU=5e-16 Radius=1.5
    g159: Circle CenterX=24.288 CenterY=-2 CenterZ=0 NormalX=0 NormalY=0 NormalZ=-1 AngleXU=5e-16 Radius=1.5
    g160: Circle CenterX=24.288 CenterY=2 CenterZ=0 NormalX=0 NormalY=0 NormalZ=-1 AngleXU=5e-16 Radius=1.5
    g161: Circle CenterX=24.288 CenterY=6 CenterZ=0 NormalX=0 NormalY=0 NormalZ=-1 AngleXU=5e-16 Radius=1.5
    g162: Circle CenterX=24.288 CenterY=10 CenterZ=0 NormalX=0 NormalY=0 NormalZ=-1 AngleXU=5e-16 Radius=1.5
    g163: Circle CenterX=20.288 CenterY=-14 CenterZ=0 NormalX=0 NormalY=0 NormalZ=-1 AngleXU=5e-16 Radius=1.5
    g164: Circle CenterX=20.288 CenterY=-10 CenterZ=0 NormalX=0 NormalY=0 NormalZ=-1 AngleXU=5e-16 Radius=1.5
    g165: Circle CenterX=20.288 CenterY=-6 CenterZ=0 NormalX=0 NormalY=0 NormalZ=-1 AngleXU=5e-16 Radius=1.5
    g166: Circle CenterX=20.288 CenterY=-2 CenterZ=0 NormalX=0 NormalY=0 NormalZ=-1 AngleXU=5e-16 Radius=1.5
    g167: Circle CenterX=20.288 CenterY=2 CenterZ=0 NormalX=0 NormalY=0 NormalZ=-1 AngleXU=5e-16 Radius=1.5
    g168: Circle CenterX=20.288 CenterY=6 CenterZ=0 NormalX=0 NormalY=0 NormalZ=-1 AngleXU=5e-16 Radius=1.5
    g169: Circle CenterX=20.288 CenterY=10 CenterZ=0 NormalX=0 NormalY=0 NormalZ=-1 AngleXU=5e-16 Radius=1.5
    g170: Circle CenterX=16.288 CenterY=-14 CenterZ=0 NormalX=0 NormalY=0 NormalZ=-1 AngleXU=5e-16 Radius=1.5
    g171: Circle CenterX=16.288 CenterY=-10 CenterZ=0 NormalX=0 NormalY=0 NormalZ=-1 AngleXU=5e-16 Radius=1.5
    g172: Circle CenterX=16.288 CenterY=-6 CenterZ=0 NormalX=0 NormalY=0 NormalZ=-1 AngleXU=5e-16 Radius=1.5
    g173: Circle CenterX=16.288 CenterY=-2 CenterZ=0 NormalX=0 NormalY=0 NormalZ=-1 AngleXU=5e-16 Radius=1.5
    g174: Circle CenterX=16.288 CenterY=2 CenterZ=0 NormalX=0 NormalY=0 NormalZ=-1 AngleXU=5e-16 Radius=1.5
    g175: Circle CenterX=16.288 CenterY=6 CenterZ=0 NormalX=0 NormalY=0 NormalZ=-1 AngleXU=5e-16 Radius=1.5
    g176: Circle CenterX=16.288 CenterY=10 CenterZ=0 NormalX=0 NormalY=0 NormalZ=-1 AngleXU=5e-16 Radius=1.5
    g177: Circle CenterX=12.288 CenterY=-14 CenterZ=0 NormalX=0 NormalY=0 NormalZ=-1 AngleXU=5e-16 Radius=1.5
    g178: Circle CenterX=12.288 CenterY=-10 CenterZ=0 NormalX=0 NormalY=0 NormalZ=-1 AngleXU=5e-16 Radius=1.5
    g179: Circle CenterX=12.288 CenterY=-6 CenterZ=0 NormalX=0 NormalY=0 NormalZ=-1 AngleXU=5e-16 Radius=1.5
    g180: Circle CenterX=12.288 CenterY=-2 CenterZ=0 NormalX=0 NormalY=0 NormalZ=-1 AngleXU=5e-16 Radius=1.5
    g181: Circle CenterX=12.288 CenterY=2 CenterZ=0 NormalX=0 NormalY=0 NormalZ=-1 AngleXU=5e-16 Radius=1.5
    g182: Circle CenterX=12.288 CenterY=6 CenterZ=0 NormalX=0 NormalY=0 NormalZ=-1 AngleXU=5e-16 Radius=1.5
    g183: Circle CenterX=12.288 CenterY=10 CenterZ=0 NormalX=0 NormalY=0 NormalZ=-1 AngleXU=5e-16 Radius=1.5
    g184: Circle CenterX=8.288 CenterY=-14 CenterZ=0 NormalX=0 NormalY=0 NormalZ=-1 AngleXU=5e-16 Radius=1.5
    g185: Circle CenterX=8.288 CenterY=-10 CenterZ=0 NormalX=0 NormalY=0 NormalZ=-1 AngleXU=5e-16 Radius=1.5
    g186: Circle CenterX=8.288 CenterY=-6 CenterZ=0 NormalX=0 NormalY=0 NormalZ=-1 AngleXU=5e-16 Radius=1.5
    g187: Circle CenterX=8.288 CenterY=-2 CenterZ=0 NormalX=0 NormalY=0 NormalZ=-1 AngleXU=5e-16 Radius=1.5
    g188: Circle CenterX=8.288 CenterY=2 CenterZ=0 NormalX=0 NormalY=0 NormalZ=-1 AngleXU=5e-16 Radius=1.5
    g189: Circle CenterX=8.288 CenterY=6 CenterZ=0 NormalX=0 NormalY=0 NormalZ=-1 AngleXU=5e-16 Radius=1.5
    g190: Circle CenterX=8.288 CenterY=10 CenterZ=0 NormalX=0 NormalY=0 NormalZ=-1 AngleXU=5e-16 Radius=1.5
    g191: Circle CenterX=4.288 CenterY=-14 CenterZ=0 NormalX=0 NormalY=0 NormalZ=-1 AngleXU=5e-16 Radius=1.5
    g192: Circle CenterX=4.288 CenterY=-10 CenterZ=0 NormalX=0 NormalY=0 NormalZ=-1 AngleXU=5e-16 Radius=1.5
    g193: Circle CenterX=4.288 CenterY=-6 CenterZ=0 NormalX=0 NormalY=0 NormalZ=-1 AngleXU=5e-16 Radius=1.5
    g194: Circle CenterX=4.288 CenterY=-2 CenterZ=0 NormalX=0 NormalY=0 NormalZ=-1 AngleXU=5e-16 Radius=1.5
    g195: Circle CenterX=4.288 CenterY=2 CenterZ=0 NormalX=0 NormalY=0 NormalZ=-1 AngleXU=5e-16 Radius=1.5
    g196: Circle CenterX=4.288 CenterY=6 CenterZ=0 NormalX=0 NormalY=0 NormalZ=-1 AngleXU=5e-16 Radius=1.5
    g197: Circle CenterX=4.288 CenterY=10 CenterZ=0 NormalX=0 NormalY=0 NormalZ=-1 AngleXU=5e-16 Radius=1.5
    g198: Circle CenterX=4.288 CenterY=14 CenterZ=0 NormalX=0 NormalY=0 NormalZ=-1 AngleXU=5e-16 Radius=1.5
    g199: LineSegment [constr] StartX=4.288 StartY=-14 StartZ=0 EndX=4.288 EndY=-10 EndZ=0
    g200: LineSegment [constr] StartX=4.288 StartY=-10 StartZ=0 EndX=4.288 EndY=-6 EndZ=0
    g201: LineSegment [constr] StartX=4.288 StartY=-2 StartZ=0 EndX=4.288 EndY=2 EndZ=0
    g202: LineSegment [constr] StartX=4.288 StartY=2 StartZ=0 EndX=4.288 EndY=6 EndZ=0
    g203: LineSegment [constr] StartX=4.288 StartY=6 StartZ=0 EndX=4.288 EndY=10 EndZ=0
    g204: LineSegment [constr] StartX=4.288 StartY=10 StartZ=0 EndX=4.288 EndY=14 EndZ=0
    g205: LineSegment [constr] StartX=4.288 StartY=14 StartZ=0 EndX=8.288 EndY=14 EndZ=0
    g206: LineSegment [constr] StartX=8.288 StartY=14 StartZ=0 EndX=12.288 EndY=14 EndZ=0
    g207: LineSegment [constr] StartX=12.288 StartY=14 StartZ=0 EndX=16.288 EndY=14 EndZ=0
    g208: LineSegment [constr] StartX=16.288 StartY=14 StartZ=0 EndX=20.288 EndY=14 EndZ=0
    g209: LineSegment [constr] StartX=20.288 StartY=14 StartZ=0 EndX=24.288 EndY=14 EndZ=0
    g210: LineSegment [constr] StartX=24.288 StartY=14 StartZ=0 EndX=28.288 EndY=14 EndZ=0
    g211: LineSegment [constr] StartX=28.288 StartY=14 StartZ=0 EndX=32.288 EndY=14 EndZ=0
    g212: LineSegment [constr] StartX=4.288 StartY=-14 StartZ=0 EndX=2.413 EndY=-14 EndZ=0
    g213: LineSegment [constr] StartX=4.288 StartY=-14 StartZ=0 EndX=4.288 EndY=-15.875 EndZ=0
    g214: LineSegment [constr] StartX=4.288 StartY=-2 StartZ=0 EndX=4.288 EndY=-6 EndZ=0
  constraints (277):
    c: Equal(g127,g129)
    c: Equal(g129,g123)
    c: Equal(g123,g125)
    c: Radius(g125) = 2.54
    c: Vertical(g126)
    c: Vertical(g130)
    c: Horizontal(g124)
    c: Tangent(g127,g128) = 1.5708
    c: Tangent(g126,g127) = 1.5708
    c: Tangent(g128,g129) = 1.5708
    c: Tangent(g129,g130) = 1.5708
    c: Tangent(g123,g130) = 1.5708
    c: Tangent(g123,g124) = 1.5708
    c: Tangent(g124,g125) = 1.5708
    c: Tangent(g125,g126) = 1.5708
    c: DistanceX(g125,g123) = 40.64
    c: DistanceY(g127,g124) = 33.02
    c: Symmetric(g124,g127,g-1)
    c: Distance(g-1,g126) = 2.032
    c: Diameter(g116) = 1.02
    c: Equal(g116,g117)
    c: Equal(g116,g115)
    c: Equal(g116,g118)
    c: Vertical(g116,g117)
    c: Vertical(g115,g118)
    c: DistanceY(g118,g115) = 2.54
    c: DistanceY(g115,g117) = 2.54
    c: DistanceY(g117,g116) = 2.54
    c: Symmetric(g117,g115,g-1)
    c: PointOnObject(g117,g-2)
    c: Diameter(g121) = 2
    c: Equal(g121,g119)
    c: Equal(g121,g120)
    c: Equal(g121,g122)
    c: Horizontal(g122,g120)
    c: Vertical(g120,g119)
    c: Horizontal(g119,g121)
    c: Symmetric(g122,g121,g-1)
    c: PointOnObject(g121,g-2)
    c: DistanceY(g122,g121) = 27.94
    c: Distance(g120,g130) = 2.032
    c: Diameter(g198) = 3
    c: Equal(g198,g141)
    c: Equal(g198,g140)
    c: Equal(g198,g139)
    c: Equal(g198,g138)
    c: Equal(g198,g137)
    c: Equal(g198,g136)
    c: Equal(g198,g135)
    c: Equal(g198,g148)
    c: Equal(g198,g155)
    c: Equal(g198,g162)
    c: Equal(g198,g169)
    c: Equal(g198,g176)
    c: Equal(g198,g183)
    c: Equal(g198,g190)
    c: Equal(g198,g197)
    c: Equal(g198,g196)
    c: Equal(g198,g189)
    c: Equal(g198,g182)
    c: Equal(g198,g175)
    c: Equal(g198,g168)
    c: Equal(g198,g161)
    c: Equal(g198,g154)
    c: Equal(g198,g147)
    c: Equal(g198,g146)
    c: Equal(g198,g153)
    c: Equal(g198,g160)
    c: Equal(g198,g167)
    c: Equal(g198,g174)
    c: Equal(g198,g181)
    c: Equal(g198,g188)
    c: Equal(g198,g195)
    c: Equal(g198,g194)
    c: Equal(g198,g187)
    c: Equal(g198,g180)
    c: Equal(g198,g173)
    c: Equal(g198,g166)
    c: Equal(g198,g159)
    c: Equal(g198,g152)
    c: Equal(g198,g145)
    c: Equal(g198,g144)
    c: Equal(g198,g151)
    c: Equal(g198,g158)
    c: Equal(g198,g165)
    c: Equal(g198,g172)
    c: Equal(g198,g179)
    c: Equal(g198,g186)
    c: Equal(g198,g193)
    c: Equal(g198,g192)
    c: Equal(g198,g185)
    c: Equal(g198,g178)
    c: Equal(g198,g171)
    c: Equal(g198,g164)
    c: Equal(g198,g157)
    c: Equal(g198,g150)
    c: Equal(g198,g143)
    c: Equal(g198,g142)
    c: Equal(g198,g149)
    c: Equal(g198,g156)
    c: Equal(g198,g163)
    c: Equal(g198,g170)
    c: Equal(g198,g177)
    c: Equal(g198,g184)
    c: Equal(g198,g191)
    c: Coincident(g199,g191)
    c: Coincident(g199,g192)
    c: Vertical(g199)
    c: Coincident(g200,g192)
    c: Coincident(g200,g193)
    c: Vertical(g200)
    c: Coincident(g201,g194)
    c: Coincident(g201,g195)
    c: Coincident(g202,g195)
    c: Coincident(g202,g196)
    c: Vertical(g202)
    c: Coincident(g203,g196)
    c: Coincident(g203,g197)
    c: Vertical(g203)
    c: Coincident(g204,g197)
    c: Coincident(g204,g198)
    c: Vertical(g204)
    c: Coincident(g205,g198)
    c: Coincident(g205,g141)
    c: Horizontal(g205)
    c: Coincident(g206,g141)
    c: Coincident(g206,g140)
    c: Horizontal(g206)
    c: Coincident(g207,g140)
    c: Coincident(g207,g139)
    c: Coincident(g208,g139)
    c: Coincident(g208,g138)
    c: Horizontal(g208)
    c: Coincident(g209,g138)
    c: Coincident(g209,g137)
    c: Coincident(g210,g137)
    c: Coincident(g210,g136)
    c: Horizontal(g210)
    c: Coincident(g211,g136)
    c: Coincident(g211,g135)
    c: Horizontal(g211)
    c: Equal(g199,g200)
    c: Equal(g201,g202)
    c: Equal(g202,g203)
    c: Equal(g203,g204)
    c: Equal(g205,g206)
    c: Equal(g206,g207)
    c: Equal(g207,g208)
    c: Equal(g208,g209)
    c: Equal(g209,g210)
    c: Equal(g210,g211)
    c: Symmetric(g194,g195,g-1)
    c: DistanceY(g201,g201) = 4
    c: DistanceX(g205,g205) = 4
    c: Vertical(g184,g185)
    c: Vertical(g185,g186)
    c: Vertical(g186,g187)
    c: Vertical(g187,g188)
    c: Vertical(g188,g189)
    c: Vertical(g189,g190)
    c: Vertical(g190,g141)
    c: Vertical(g140,g183)
    c: Vertical(g183,g182)
    c: Vertical(g182,g181)
    c: Vertical(g181,g180)
    c: Vertical(g180,g179)
    c: Vertical(g179,g178)
    c: Vertical(g178,g177)
    c: Vertical(g139,g176)
    c: Vertical(g176,g175)
    c: Vertical(g175,g174)
    c: Vertical(g174,g173)
    c: Vertical(g173,g172)
    c: Vertical(g172,g171)
    c: Vertical(g171,g170)
    c: Vertical(g138,g169)
    c: Vertical(g169,g168)
    c: Vertical(g168,g167)
    c: Vertical(g167,g166)
    c: Vertical(g166,g165)
    c: Vertical(g165,g164)
    c: Vertical(g164,g163)
    c: Vertical(g137,g162)
    c: Vertical(g162,g161)
    c: Vertical(g161,g160)
    c: Vertical(g160,g159)
    c: Vertical(g159,g158)
    c: Vertical(g158,g157)
    c: Vertical(g157,g156)
    c: Vertical(g136,g155)
    c: Vertical(g155,g154)
    c: Vertical(g154,g153)
    c: Vertical(g153,g152)
    c: Vertical(g152,g151)
    c: Vertical(g151,g150)
    c: Vertical(g150,g149)
    c: Vertical(g135,g148)
    c: Vertical(g148,g147)
    c: Vertical(g147,g146)
    c: Vertical(g146,g145)
    c: Vertical(g145,g144)
    c: Vertical(g144,g143)
    c: Vertical(g143,g142)
    c: Horizontal(g197,g190)
    c: Horizontal(g190,g183)
    c: Horizontal(g183,g176)
    c: Horizontal(g176,g169)
    c: Horizontal(g169,g162)
    c: Horizontal(g162,g155)
    c: Horizontal(g155,g148)
    c: Horizontal(g196,g189)
    c: Horizontal(g189,g182)
    c: Horizontal(g182,g175)
    c: Horizontal(g175,g168)
    c: Horizontal(g168,g161)
    c: Horizontal(g161,g154)
    c: Horizontal(g154,g147)
    c: Horizontal(g195,g188)
    c: Horizontal(g188,g181)
    c: Horizontal(g181,g174)
    c: Horizontal(g174,g167)
    c: Horizontal(g167,g160)
    c: Horizontal(g160,g153)
    c: Horizontal(g153,g146)
    c: Horizontal(g194,g187)
    c: Horizontal(g187,g180)
    c: Horizontal(g180,g173)
    c: Horizontal(g173,g166)
    c: Horizontal(g166,g159)
    c: Horizontal(g159,g152)
    c: Horizontal(g152,g145)
    c: Horizontal(g193,g186)
    c: Horizontal(g186,g179)
    c: Horizontal(g179,g172)
    c: Horizontal(g172,g165)
    c: Horizontal(g165,g158)
    c: Horizontal(g158,g151)
    c: Horizontal(g151,g144)
    c: Horizontal(g192,g185)
    c: Horizontal(g185,g178)
    c: Horizontal(g178,g171)
    c: Horizontal(g171,g164)
    c: Horizontal(g164,g157)
    c: Horizontal(g157,g150)
    c: Horizontal(g150,g143)
    c: Horizontal(g191,g184)
    c: Horizontal(g184,g177)
    c: Horizontal(g177,g170)
    c: Horizontal(g170,g163)
    c: Horizontal(g163,g156)
    c: Horizontal(g156,g149)
    c: Horizontal(g149,g142)
    c: Coincident(g131,g132)
    c: Horizontal(g131)
    c: Coincident(g132,g133)
    c: Horizontal(g133)
    c: Coincident(g133,g134)
    c: Vertical(g134)
    c: Coincident(g131,g134)
    c: Equal(g132,g131)
    c: DistanceY(g132,g132) = 31.75
    c: Symmetric(g131,g132,g-1)
    c: Coincident(g212,g191)
    c: PointOnObject(g212,g132)
    c: Coincident(g213,g191)
    c: PointOnObject(g213,g133)
    c: Vertical(g213)
    c: Horizontal(g212)
    c: Equal(g212,g213)
    c: DistanceX(g212,g212) = 1.875
    c: Coincident(g214,g194)
    c: Coincident(g214,g193)
    c: Vertical(g214)
    c: Horizontal(g207)
    c: Horizontal(g209)
    c: DistanceX(g125,g131) = 4.445
    c: Equal(g201,g214)
FEATURE [App::DocumentObjectGroup] Group  label="LED_matrix_8x8"
  ClaimAllChildren = true
  ExportMode = 1
  Group = -> [Sketch009,Sketch008,Sketch006,Text001,Text,Sketch002,Sketch010]
  TreeRank = 2145
  _GroupVersion = 1
